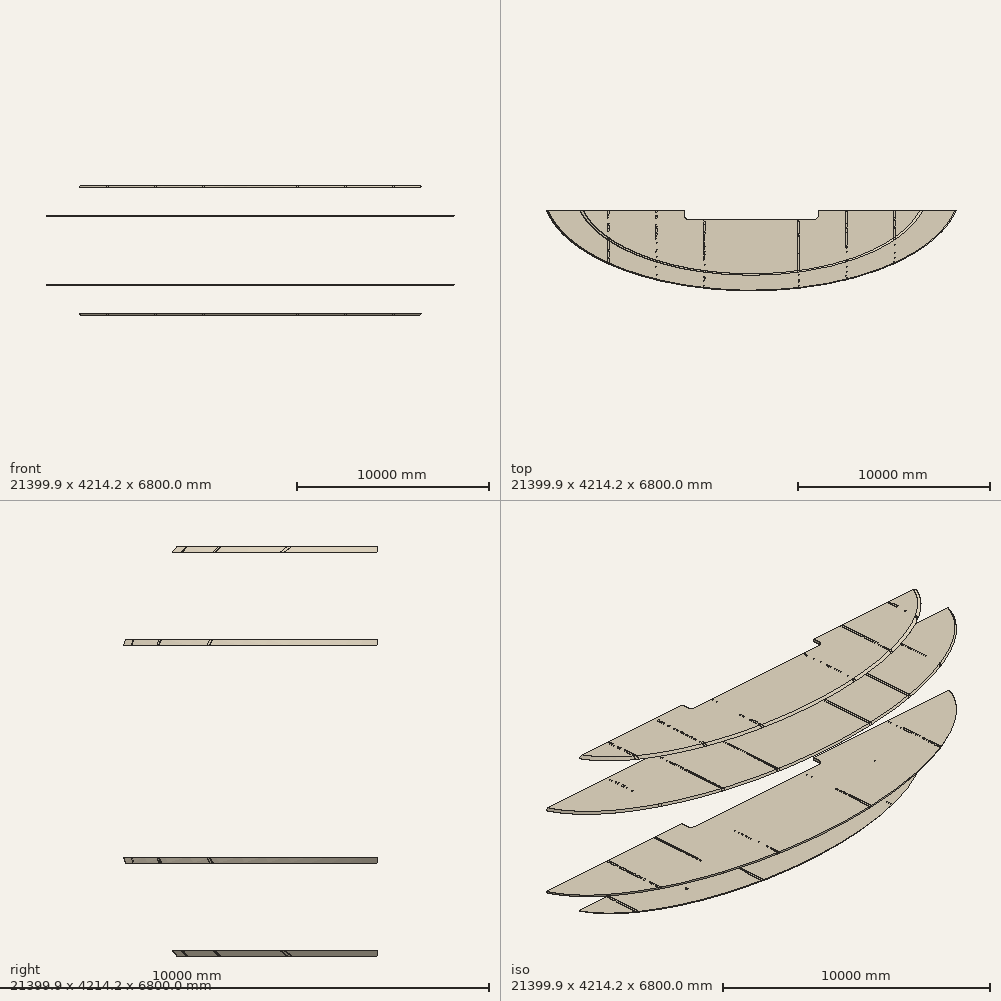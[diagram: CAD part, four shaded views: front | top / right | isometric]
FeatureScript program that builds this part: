
annotation { "Feature Type Name" : "Feature", "Feature Type Description" : "" }
export const myFeature = defineFeature(function(context is Context, id is Id, definition is map)
    precondition{}
    {
        {
            var Q0;
            Q0=qCreatedBy(makeId("Front.planeOp"),FACE);
            var sketch = newSketch(context, id + "F0", { "sketchPlane" : qUnion([Q0])});
            skEllipticalArc(sketch, "E0", {});
            skLineSegment(sketch, "E1", {"start": v(0, 0) * mm, "end": v(8999.75, 0) * mm});
            skLineSegment(sketch, "E2", {"start": v(-11500, 0) * mm, "end": v(11500, 0) * mm});
            const initialGuessF0  = {"E0": [0, 0, 0, 1, 5.5, 11.5, 4.71238898038469, 1.5707963267948966]};
            skSetInitialGuess(sketch, initialGuessF0);
            skSolve(sketch);
        }
        {
            var Q0;
            {var subQ1=sQuery(id+"F0.wireOp",EDGE,"E0");Q0=makeQuery(id+"F0.imprint","IMPRINT",FACE,{"disambiguationData":[TD([[makeQuery(id+"F0.imprint","IMPRINT",EDGE,{"derivedFrom":subQ1}),1.0]])]});}
            var Q1;
            Q1=sQuery(id+"F0.wireOp",EDGE,"E1");
            revolve(context, id + "F1", {"entities" : qUnion([Q0]), "axis" : qUnion([Q1]), "revolveType" : RevolveType.FULL});
        }
        {
            var Q0;
            Q0=qCreatedBy(makeId("Top.planeOp"),FACE);
            var sketch = newSketch(context, id + "F2", { "sketchPlane" : qUnion([Q0])});
            skLineSegment(sketch, "E3.bottom", {"start": v(-12000, 6000) * mm, "end": v(12000, 6000) * mm});
            skLineSegment(sketch, "E3.top", {"start": v(-12000, -1000) * mm, "end": v(12000, -1000) * mm});
            skLineSegment(sketch, "E3.left", {"start": v(-12000, 6000) * mm, "end": v(-12000, -1000) * mm});
            skLineSegment(sketch, "E3.right", {"start": v(12000, 6000) * mm, "end": v(12000, -1000) * mm});
            skSolve(sketch);
        }
        {
            var Q0;
            Q0=makeQuery(id+"F2.imprint","IMPRINT",FACE,{"disambiguationData":[TD([[makeQuery(id+"F2.imprint","IMPRINT",EDGE,{"derivedFrom":sQuery(id+"F2.wireOp",EDGE,"E3.bottom")}),-1.0]])]});
            extrude(context, id + "F3", {"entities" : qUnion([Q0]), "operationType" : NewBodyOperationType.REMOVE, "endBound" : BoundingType.SYMMETRIC, "oppositeDirection" : true, "depth" : 14000 * mm});
        }
        {
            var Q0;
            Q0=qCreatedBy(makeId("Front.planeOp"),FACE);
            var sketch = newSketch(context, id + "F4", { "sketchPlane" : qUnion([Q0])});
            skLineSegment(sketch, "E4", {"start": v(0, 0) * mm, "end": v(0, 6585.44) * mm, "construction": true});
            skLineSegment(sketch, "E5", {"start": v(2500, 6602.1) * mm, "end": v(2500, -6465.32) * mm});
            skLineSegment(sketch, "E6", {"start": v(5000, 6568.77) * mm, "end": v(5000, -6415.32) * mm});
            skLineSegment(sketch, "E7", {"start": v(7500, 6535.43) * mm, "end": v(7500, -6381.98) * mm});
            skLineSegment(sketch, "E8.0", {"start": v(2400, 6602.1) * mm, "end": v(2400, -6465.32) * mm});
            skLineSegment(sketch, "E9.0", {"start": v(4900, 6568.77) * mm, "end": v(4900, -6415.32) * mm});
            skLineSegment(sketch, "E10.0", {"start": v(7400, 6535.43) * mm, "end": v(7400, -6381.98) * mm});
            skLineSegment(sketch, "E11", {"start": v(2400, 6602.1) * mm, "end": v(2500, 6602.1) * mm});
            skLineSegment(sketch, "E12", {"start": v(4900, 6568.77) * mm, "end": v(5000, 6568.77) * mm});
            skLineSegment(sketch, "E13", {"start": v(7400, 6535.43) * mm, "end": v(7500, 6535.43) * mm});
            skLineSegment(sketch, "E14", {"start": v(2400, -6465.32) * mm, "end": v(2500, -6465.32) * mm});
            skLineSegment(sketch, "E15", {"start": v(4900, -6415.32) * mm, "end": v(5000, -6415.32) * mm});
            skLineSegment(sketch, "E16", {"start": v(7400, -6381.98) * mm, "end": v(7500, -6381.98) * mm});
            skLineSegment(sketch, "E17.MirrorCS", {"start": v(-7400, 6535.43) * mm, "end": v(-7400, -6381.98) * mm});
            skLineSegment(sketch, "E18.MirrorCS", {"start": v(-4900, 6568.77) * mm, "end": v(-4900, -6415.32) * mm});
            skLineSegment(sketch, "E19.MirrorCS", {"start": v(-2400, 6602.1) * mm, "end": v(-2400, -6465.32) * mm});
            skLineSegment(sketch, "E20.MirrorCS", {"start": v(-7500, 6535.43) * mm, "end": v(-7500, -6381.98) * mm});
            skLineSegment(sketch, "E21.MirrorCS", {"start": v(-5000, 6568.77) * mm, "end": v(-5000, -6415.32) * mm});
            skLineSegment(sketch, "E22.MirrorCS", {"start": v(-2500, 6602.1) * mm, "end": v(-2500, -6465.32) * mm});
            skLineSegment(sketch, "E23.MirrorCS", {"start": v(-2400, 6602.1) * mm, "end": v(-2500, 6602.1) * mm});
            skLineSegment(sketch, "E24.MirrorCS", {"start": v(-4900, 6568.77) * mm, "end": v(-5000, 6568.77) * mm});
            skLineSegment(sketch, "E25.MirrorCS", {"start": v(-7400, 6535.43) * mm, "end": v(-7500, 6535.43) * mm});
            skLineSegment(sketch, "E26.MirrorCS", {"start": v(-2400, -6465.32) * mm, "end": v(-2500, -6465.32) * mm});
            skLineSegment(sketch, "E27.MirrorCS", {"start": v(-4900, -6415.32) * mm, "end": v(-5000, -6415.32) * mm});
            skLineSegment(sketch, "E28.MirrorCS", {"start": v(-7400, -6381.98) * mm, "end": v(-7500, -6381.98) * mm});
            skSolve(sketch);
        }
        {
            var Q0;
            Q0=qCreatedBy(makeId("Front.planeOp"),FACE);
            var sketch = newSketch(context, id + "F5", { "sketchPlane" : qUnion([Q0])});
            skLineSegment(sketch, "E29", {"start": v(0, 0) * mm, "end": v(8074.7, 0) * mm, "construction": true});
            skLineSegment(sketch, "E30", {"start": v(-12000, 1850) * mm, "end": v(12000, 1850) * mm});
            skLineSegment(sketch, "E31", {"start": v(-12000, 3400) * mm, "end": v(12000, 3400) * mm});
            skLineSegment(sketch, "E32.0", {"start": v(-12000, 1750) * mm, "end": v(12000, 1750) * mm});
            skLineSegment(sketch, "E33.0", {"start": v(-12000, 3300) * mm, "end": v(12000, 3300) * mm});
            skLineSegment(sketch, "E34", {"start": v(-12000, 3400) * mm, "end": v(-12000, 3300) * mm});
            skLineSegment(sketch, "E35", {"start": v(-12000, 1850) * mm, "end": v(-12000, 1750) * mm});
            skLineSegment(sketch, "E36", {"start": v(12000, 3400) * mm, "end": v(12000, 3300) * mm});
            skLineSegment(sketch, "E37", {"start": v(12000, 1850) * mm, "end": v(12000, 1750) * mm});
            skLineSegment(sketch, "E38.MirrorCS", {"start": v(-12000, -3400) * mm, "end": v(12000, -3400) * mm});
            skLineSegment(sketch, "E39.MirrorCS", {"start": v(-12000, -1850) * mm, "end": v(12000, -1850) * mm});
            skLineSegment(sketch, "E40.MirrorCS", {"start": v(-12000, -1750) * mm, "end": v(12000, -1750) * mm});
            skLineSegment(sketch, "E41.MirrorCS", {"start": v(-12000, -3300) * mm, "end": v(12000, -3300) * mm});
            skLineSegment(sketch, "E42.MirrorCS", {"start": v(12000, -1850) * mm, "end": v(12000, -1750) * mm});
            skLineSegment(sketch, "E43.MirrorCS", {"start": v(12000, -3400) * mm, "end": v(12000, -3300) * mm});
            skLineSegment(sketch, "E44.MirrorCS", {"start": v(-12000, -1850) * mm, "end": v(-12000, -1750) * mm});
            skLineSegment(sketch, "E45.MirrorCS", {"start": v(-12000, -3400) * mm, "end": v(-12000, -3300) * mm});
            skSolve(sketch);
        }
        {
            var Q0;
            Q0=makeQuery(id+"F4.imprint","IMPRINT",FACE,{"disambiguationData":[TD([[makeQuery(id+"F4.imprint","IMPRINT",EDGE,{"derivedFrom":sQuery(id+"F4.wireOp",EDGE,"E17.MirrorCS")}),-1.0]])]});
            var Q1;
            Q1=makeQuery(id+"F4.imprint","IMPRINT",FACE,{"disambiguationData":[TD([[makeQuery(id+"F4.imprint","IMPRINT",EDGE,{"derivedFrom":sQuery(id+"F4.wireOp",EDGE,"E7")}),-1.0]])]});
            var Q2;
            Q2=makeQuery(id+"F4.imprint","IMPRINT",FACE,{"disambiguationData":[TD([[makeQuery(id+"F4.imprint","IMPRINT",EDGE,{"derivedFrom":sQuery(id+"F4.wireOp",EDGE,"E6")}),-1.0]])]});
            var Q3;
            Q3=makeQuery(id+"F4.imprint","IMPRINT",FACE,{"disambiguationData":[TD([[makeQuery(id+"F4.imprint","IMPRINT",EDGE,{"derivedFrom":sQuery(id+"F4.wireOp",EDGE,"E5")}),-1.0]])]});
            var Q4;
            Q4=makeQuery(id+"F4.imprint","IMPRINT",FACE,{"disambiguationData":[TD([[makeQuery(id+"F4.imprint","IMPRINT",EDGE,{"derivedFrom":sQuery(id+"F4.wireOp",EDGE,"E18.MirrorCS")}),-1.0]])]});
            var Q5;
            Q5=makeQuery(id+"F4.imprint","IMPRINT",FACE,{"disambiguationData":[TD([[makeQuery(id+"F4.imprint","IMPRINT",EDGE,{"derivedFrom":sQuery(id+"F4.wireOp",EDGE,"E19.MirrorCS")}),-1.0]])]});
            extrude(context, id + "F6", {"entities" : qUnion([Q0, Q1, Q2, Q3, Q4, Q5]), "operationType" : NewBodyOperationType.INTERSECT, "depth" : 6000 * mm});
        }
        {
            var Q0;
            Q0 = qSketchRegion(id + "F0", true);
            var Q1;
            Q1=sQuery(id+"F5.wireOp",EDGE,"E29");
            revolve(context, id + "F7", {"entities" : qUnion([Q0]), "axis" : qUnion([Q1]), "revolveType" : RevolveType.FULL});
        }
        {
            var Q0;
            Q0 = qSketchRegion(id + "F2", true);
            extrude(context, id + "F8", {"entities" : qUnion([Q0]), "operationType" : NewBodyOperationType.REMOVE, "endBound" : BoundingType.SYMMETRIC, "oppositeDirection" : true, "depth" : 12000 * mm});
        }
        {
            var Q0;
            Q0 = qSketchRegion(id + "F5", true);
            extrude(context, id + "F9", {"entities" : qUnion([Q0]), "operationType" : NewBodyOperationType.INTERSECT, "depth" : 6000 * mm});
        }
        {
            var Q0;
            Q0=qCreatedBy(makeId("Top.planeOp"),FACE);
            var sketch = newSketch(context, id + "F10", { "sketchPlane" : qUnion([Q0])});
            skLineSegment(sketch, "E46.bottom", {"start": v(-3500, -500) * mm, "end": v(3500, -500) * mm});
            skLineSegment(sketch, "E46.top", {"start": v(-3300, -1500) * mm, "end": v(3300, -1500) * mm});
            skLineSegment(sketch, "E46.left", {"start": v(-3500, -500) * mm, "end": v(-3500, -1300) * mm});
            skLineSegment(sketch, "E46.right", {"start": v(3500, -500) * mm, "end": v(3500, -1300) * mm});
            skLineSegment(sketch, "E47.left", {"start": v(-3500, -500) * mm, "end": v(-3500, -500) * mm});
            skLineSegment(sketch, "E47.right", {"start": v(3500, -500) * mm, "end": v(3500, -500) * mm});
            skPoint(sketch, "E48.visualSharp", {"position": v(-3500, -1500) * mm});
            skArc(sketch, "E48.filletArc", {"start": v(-3500, -1300) * mm, "mid": v(-3441.42, -1441.42) * mm, "end": v(-3300, -1500) * mm});
            skPoint(sketch, "E49.visualSharp", {"position": v(3500, -1500) * mm});
            skArc(sketch, "E49.filletArc", {"start": v(3300, -1500) * mm, "mid": v(3441.42, -1441.42) * mm, "end": v(3500, -1300) * mm});
            skSolve(sketch);
        }
        {
            var Q0;
            Q0=makeQuery(id+"F10.imprint","IMPRINT",FACE,{"disambiguationData":[TD([[makeQuery(id+"F10.imprint","IMPRINT",EDGE,{"derivedFrom":sQuery(id+"F10.wireOp",EDGE,"E46.top")}),1.0]])]});
            extrude(context, id + "F11", {"entities" : qUnion([Q0]), "operationType" : NewBodyOperationType.REMOVE, "endBound" : BoundingType.SYMMETRIC, "oppositeDirection" : true, "depth" : 13000 * mm});
        }
    });
